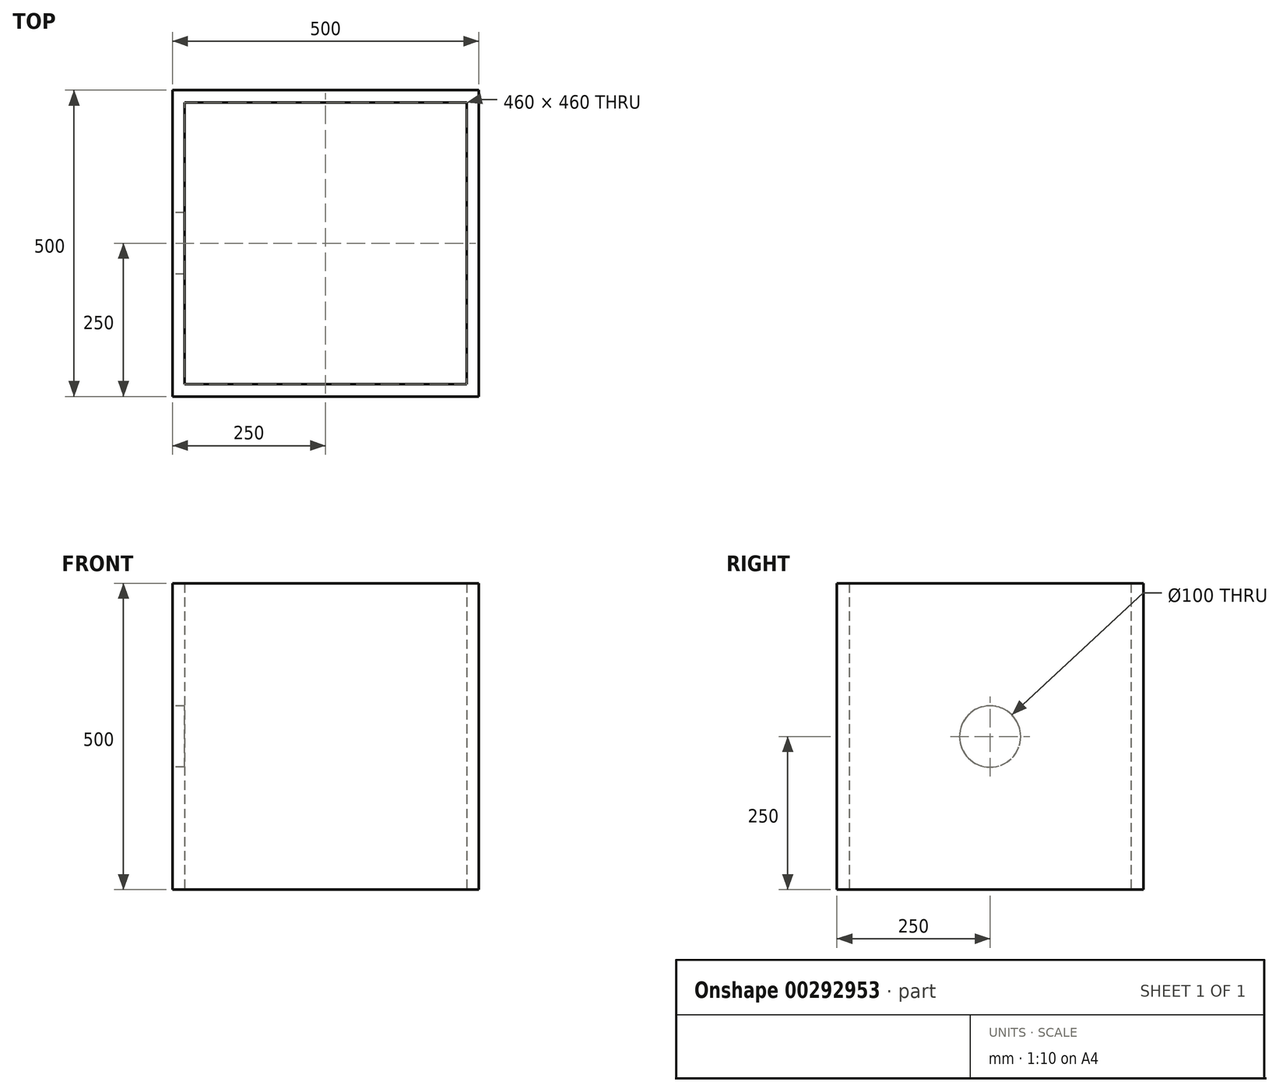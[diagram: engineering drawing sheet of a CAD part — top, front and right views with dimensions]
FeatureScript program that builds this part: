
annotation { "Feature Type Name" : "Feature", "Feature Type Description" : "" }
export const myFeature = defineFeature(function(context is Context, id is Id, definition is map)
    precondition{}
    {
        {
            var Q0;
            Q0=qCreatedBy(makeId("Top.planeOp"),FACE);
            var sketch = newSketch(context, id + "F0", { "sketchPlane" : qUnion([Q0])});
            skLineSegment(sketch, "E0.bottom", {"start": v(250, 250) * mm, "end": v(-250, 250) * mm});
            skLineSegment(sketch, "E0.top", {"start": v(250, -250) * mm, "end": v(-250, -250) * mm});
            skLineSegment(sketch, "E0.left", {"start": v(250, 250) * mm, "end": v(250, -250) * mm});
            skLineSegment(sketch, "E0.right", {"start": v(-250, 250) * mm, "end": v(-250, -250) * mm});
            skPoint(sketch, "E0.middle", {"position": v(0, 0) * mm});
            skLineSegment(sketch, "E1.0", {"start": v(230, -230) * mm, "end": v(-230, -230) * mm});
            skLineSegment(sketch, "E1.1", {"start": v(230, 230) * mm, "end": v(230, -230) * mm});
            skLineSegment(sketch, "E1.2", {"start": v(230, 230) * mm, "end": v(-230, 230) * mm});
            skLineSegment(sketch, "E1.3", {"start": v(-230, 230) * mm, "end": v(-230, -230) * mm});
            skSolve(sketch);
        }
        {
            var Q0;
            Q0=makeQuery(id+"F0.imprint","IMPRINT",FACE,{"disambiguationData":[TD([[makeQuery(id+"F0.imprint","IMPRINT",EDGE,{"derivedFrom":sQuery(id+"F0.wireOp",EDGE,"E0.bottom")}),1.0]])]});
            extrude(context, id + "F1", {"entities" : qUnion([Q0]), "depth" : 500 * mm});
        }
        {
            var Q0;
            Q0=makeQuery(id+"F1.opExtrude","SWEPT_FACE",FACE,{"disambiguationData":[OSD([sQuery(id+"F0.wireOp",EDGE,"E0.right")])]});
            var sketch = newSketch(context, id + "F2", { "sketchPlane" : qUnion([Q0])});
            skCircle(sketch, "E2", {"center": v(0, 250) * mm, "radius": 50 * mm});
            skPoint(sketch, "E2.centerSnap0", {"position": v(-250, 250) * mm});
            skSolve(sketch);
        }
        {
            var Q0;
            Q0=makeQuery(id+"F2.imprint","IMPRINT",FACE,{"disambiguationData":[TD([[makeQuery(id+"F2.imprint","IMPRINT",EDGE,{"derivedFrom":sQuery(id+"F2.wireOp",EDGE,"E2")}),1.0]])]});
            extrude(context, id + "F3", {"entities" : qUnion([Q0]), "operationType" : NewBodyOperationType.REMOVE, "endBound" : BoundingType.UP_TO_NEXT, "oppositeDirection" : true, "depth" : 20 * mm});
        }
    });
